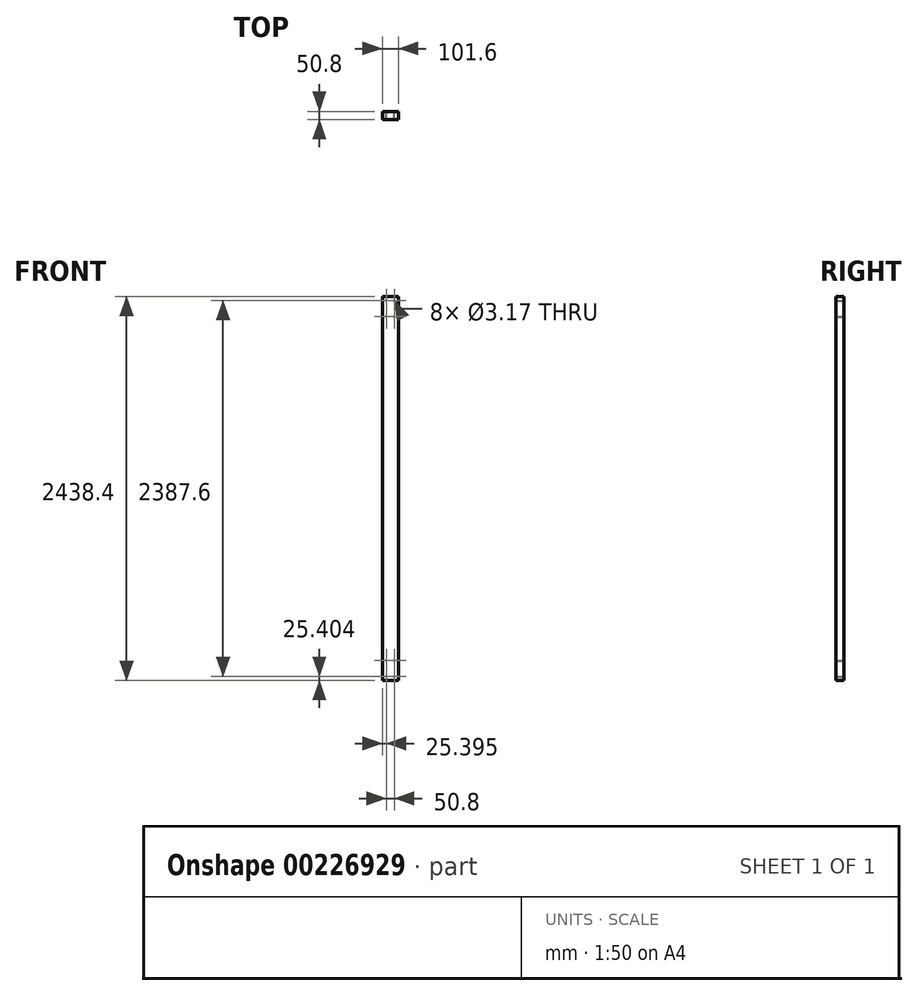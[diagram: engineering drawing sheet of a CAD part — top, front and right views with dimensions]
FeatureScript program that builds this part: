
annotation { "Feature Type Name" : "Feature", "Feature Type Description" : "" }
export const myFeature = defineFeature(function(context is Context, id is Id, definition is map)
    precondition{}
    {
        {
            var Q0;
            Q0=qCreatedBy(makeId("Front.planeOp"),FACE);
            var sketch = newSketch(context, id + "F0", { "sketchPlane" : qUnion([Q0])});
            skLineSegment(sketch, "E0.bottom", {"start": v(-55.04, 2395.4) * mm, "end": v(46.56, 2395.4) * mm});
            skLineSegment(sketch, "E0.top", {"start": v(-55.04, -43) * mm, "end": v(46.56, -43) * mm});
            skLineSegment(sketch, "E0.left", {"start": v(-55.04, 2395.4) * mm, "end": v(-55.04, -43) * mm});
            skLineSegment(sketch, "E0.right", {"start": v(46.56, 2395.4) * mm, "end": v(46.56, -43) * mm});
            skCircle(sketch, "E1", {"center": v(-29.64, 2370) * mm, "radius": 1.59 * mm});
            skCircle(sketch, "E2", {"center": v(21.16, 2370) * mm, "radius": 1.59 * mm});
            skCircle(sketch, "E3", {"center": v(-29.64, 2268.4) * mm, "radius": 1.59 * mm});
            skCircle(sketch, "E4", {"center": v(21.16, 2268.4) * mm, "radius": 1.59 * mm});
            skCircle(sketch, "E5", {"center": v(-29.64, -17.6) * mm, "radius": 1.59 * mm});
            skCircle(sketch, "E6", {"center": v(21.16, -17.6) * mm, "radius": 1.59 * mm});
            skCircle(sketch, "E7", {"center": v(-29.64, 84) * mm, "radius": 1.59 * mm});
            skCircle(sketch, "E8", {"center": v(21.16, 84) * mm, "radius": 1.59 * mm});
            skSolve(sketch);
        }
        {
            var Q0;
            Q0=makeQuery(id+"F0.imprint","IMPRINT",FACE,{"disambiguationData":[TD([[makeQuery(id+"F0.imprint","IMPRINT",EDGE,{"derivedFrom":sQuery(id+"F0.wireOp",EDGE,"E0.bottom")}),-1.0]])]});
            extrude(context, id + "F1", {"entities" : qUnion([Q0]), "depth" : 50.8 * mm});
        }
    });
